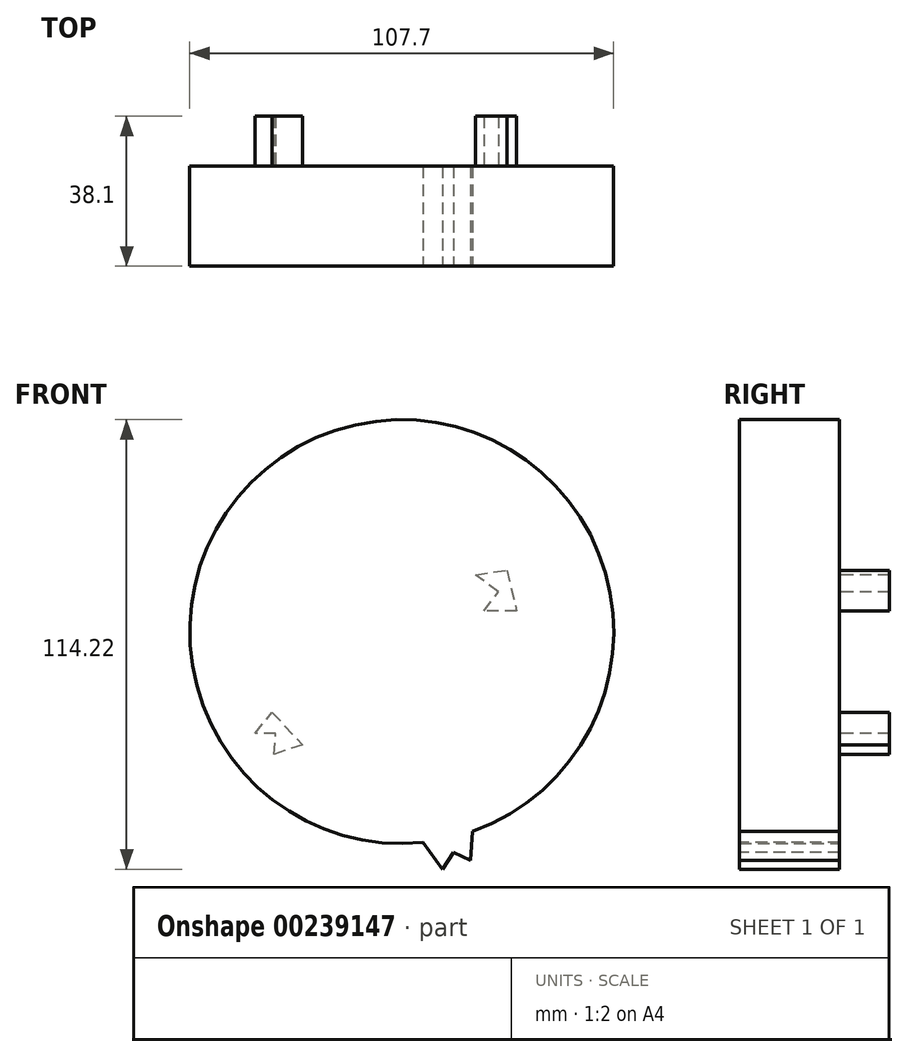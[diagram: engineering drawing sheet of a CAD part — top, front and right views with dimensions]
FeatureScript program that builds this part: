
annotation { "Feature Type Name" : "Feature", "Feature Type Description" : "" }
export const myFeature = defineFeature(function(context is Context, id is Id, definition is map)
    precondition{}
    {
        {
            var Q0;
            Q0=qCreatedBy(makeId("Front.planeOp"),FACE);
            var sketch = newSketch(context, id + "F0", { "sketchPlane" : qUnion([Q0])});
            skCircle(sketch, "E0", {"center": v(0, 0) * mm, "radius": 53.85 * mm});
            skSolve(sketch);
        }
        {
            var Q0;
            Q0 = qSketchRegion(id + "F0", true);
            extrude(context, id + "F1", {"entities" : qUnion([Q0]), "endBound" : BoundingType.SYMMETRIC, "depth" : 25.4 * mm});
        }
        {
            var Q0;
            Q0=makeQuery(id+"F1.opExtrude","CAP_FACE",FACE,{"disambiguationData":[OSD([sQuery(id+"F0.wireOp",EDGE,"E0")])],"isStart":false});
            var sketch = newSketch(context, id + "F2", { "sketchPlane" : qUnion([Q0])});
            skLineSegment(sketch, "E1", {"start": v(17.98, -50.76) * mm, "end": v(5.43, -53.58) * mm});
            skLineSegment(sketch, "E2", {"start": v(5.43, -53.58) * mm, "end": v(10.38, -60.37) * mm});
            skLineSegment(sketch, "E3", {"start": v(10.38, -60.37) * mm, "end": v(13.2, -56.1) * mm});
            skLineSegment(sketch, "E4", {"start": v(13.2, -56.1) * mm, "end": v(17.47, -58.15) * mm});
            skLineSegment(sketch, "E5", {"start": v(17.47, -58.15) * mm, "end": v(17.98, -50.76) * mm});
            skSolve(sketch);
        }
        {
            var Q0;
            Q0 = qSketchRegion(id + "F2", true);
            var Q1;
            Q1=makeQuery(id+"F1.opExtrude","CAP_FACE",FACE,{"disambiguationData":[OSD([sQuery(id+"F0.wireOp",EDGE,"E0")])],"isStart":true});
            extrude(context, id + "F3", {"entities" : qUnion([Q0]), "operationType" : NewBodyOperationType.ADD, "endBound" : BoundingType.UP_TO_SURFACE, "oppositeDirection" : true, "endBoundEntityFace" : qUnion([Q1]), "depth" : 25.4 * mm});
        }
        {
            var Q0;
            {var subQ0=sQuery(id+"F0.wireOp",EDGE,"E0");Q0=makeQuery(id+"FucFUCRXuMYFfXz_1.19.F3.boolean.opBoolean","MERGE",FACE,{"derivedFrom":[makeQuery(id+"FucFUCRXuMYFfXz_1.18.F3.boolean.opBoolean","MERGE",FACE,{"derivedFrom":[makeQuery(id+"FucFUCRXuMYFfXz_1.17.F3.boolean.opBoolean","MERGE",FACE,{"derivedFrom":[makeQuery(id+"FucFUCRXuMYFfXz_1.16.F3.boolean.opBoolean","MERGE",FACE,{"derivedFrom":[makeQuery(id+"FucFUCRXuMYFfXz_1.15.F3.boolean.opBoolean","MERGE",FACE,{"derivedFrom":[makeQuery(id+"FucFUCRXuMYFfXz_1.14.F3.boolean.opBoolean","MERGE",FACE,{"derivedFrom":[makeQuery(id+"FucFUCRXuMYFfXz_1.13.F3.boolean.opBoolean","MERGE",FACE,{"derivedFrom":[makeQuery(id+"FucFUCRXuMYFfXz_1.12.F3.boolean.opBoolean","MERGE",FACE,{"derivedFrom":[makeQuery(id+"FucFUCRXuMYFfXz_1.11.F3.boolean.opBoolean","MERGE",FACE,{"derivedFrom":[makeQuery(id+"FucFUCRXuMYFfXz_1.10.F3.boolean.opBoolean","MERGE",FACE,{"derivedFrom":[makeQuery(id+"FucFUCRXuMYFfXz_1.9.F3.boolean.opBoolean","MERGE",FACE,{"derivedFrom":[makeQuery(id+"FucFUCRXuMYFfXz_1.8.F3.boolean.opBoolean","MERGE",FACE,{"derivedFrom":[makeQuery(id+"FucFUCRXuMYFfXz_1.7.F3.boolean.opBoolean","MERGE",FACE,{"derivedFrom":[makeQuery(id+"FucFUCRXuMYFfXz_1.6.F3.boolean.opBoolean","MERGE",FACE,{"derivedFrom":[makeQuery(id+"FucFUCRXuMYFfXz_1.5.F3.boolean.opBoolean","MERGE",FACE,{"derivedFrom":[makeQuery(id+"FucFUCRXuMYFfXz_1.4.F3.boolean.opBoolean","MERGE",FACE,{"derivedFrom":[makeQuery(id+"FucFUCRXuMYFfXz_1.3.F3.boolean.opBoolean","MERGE",FACE,{"derivedFrom":[makeQuery(id+"FucFUCRXuMYFfXz_1.2.F3.boolean.opBoolean","MERGE",FACE,{"derivedFrom":[makeQuery(id+"FucFUCRXuMYFfXz_1.1.F3.boolean.opBoolean","MERGE",FACE,{"derivedFrom":[makeQuery(id+"F3.boolean.opBoolean","MERGE",FACE,{"derivedFrom":[makeQuery(id+"F1.opExtrude","CAP_FACE",FACE,{"disambiguationData":[OSD([subQ0])],"isStart":true}),makeQuery(id+"F3.opExtrude","CAP_FACE",FACE,{"disambiguationData":[OSD([subQ0])],"isStart":false})]}),makeQuery(id+"FucFUCRXuMYFfXz_1.1.F3.opExtrude","CAP_FACE",FACE,{"disambiguationData":[OSD([subQ0])],"isStart":false})]}),makeQuery(id+"FucFUCRXuMYFfXz_1.2.F3.opExtrude","CAP_FACE",FACE,{"disambiguationData":[OSD([subQ0])],"isStart":false})]}),makeQuery(id+"FucFUCRXuMYFfXz_1.3.F3.opExtrude","CAP_FACE",FACE,{"disambiguationData":[OSD([subQ0])],"isStart":false})]}),makeQuery(id+"FucFUCRXuMYFfXz_1.4.F3.opExtrude","CAP_FACE",FACE,{"disambiguationData":[OSD([subQ0])],"isStart":false})]}),makeQuery(id+"FucFUCRXuMYFfXz_1.5.F3.opExtrude","CAP_FACE",FACE,{"disambiguationData":[OSD([subQ0])],"isStart":false})]}),makeQuery(id+"FucFUCRXuMYFfXz_1.6.F3.opExtrude","CAP_FACE",FACE,{"disambiguationData":[OSD([subQ0])],"isStart":false})]}),makeQuery(id+"FucFUCRXuMYFfXz_1.7.F3.opExtrude","CAP_FACE",FACE,{"disambiguationData":[OSD([subQ0])],"isStart":false})]}),makeQuery(id+"FucFUCRXuMYFfXz_1.8.F3.opExtrude","CAP_FACE",FACE,{"disambiguationData":[OSD([subQ0])],"isStart":false})]}),makeQuery(id+"FucFUCRXuMYFfXz_1.9.F3.opExtrude","CAP_FACE",FACE,{"disambiguationData":[OSD([subQ0])],"isStart":false})]}),makeQuery(id+"FucFUCRXuMYFfXz_1.10.F3.opExtrude","CAP_FACE",FACE,{"disambiguationData":[OSD([subQ0])],"isStart":false})]}),makeQuery(id+"FucFUCRXuMYFfXz_1.11.F3.opExtrude","CAP_FACE",FACE,{"disambiguationData":[OSD([subQ0])],"isStart":false})]}),makeQuery(id+"FucFUCRXuMYFfXz_1.12.F3.opExtrude","CAP_FACE",FACE,{"disambiguationData":[OSD([subQ0])],"isStart":false})]}),makeQuery(id+"FucFUCRXuMYFfXz_1.13.F3.opExtrude","CAP_FACE",FACE,{"disambiguationData":[OSD([subQ0])],"isStart":false})]}),makeQuery(id+"FucFUCRXuMYFfXz_1.14.F3.opExtrude","CAP_FACE",FACE,{"disambiguationData":[OSD([subQ0])],"isStart":false})]}),makeQuery(id+"FucFUCRXuMYFfXz_1.15.F3.opExtrude","CAP_FACE",FACE,{"disambiguationData":[OSD([subQ0])],"isStart":false})]}),makeQuery(id+"FucFUCRXuMYFfXz_1.16.F3.opExtrude","CAP_FACE",FACE,{"disambiguationData":[OSD([subQ0])],"isStart":false})]}),makeQuery(id+"FucFUCRXuMYFfXz_1.17.F3.opExtrude","CAP_FACE",FACE,{"disambiguationData":[OSD([subQ0])],"isStart":false})]}),makeQuery(id+"FucFUCRXuMYFfXz_1.18.F3.opExtrude","CAP_FACE",FACE,{"disambiguationData":[OSD([subQ0])],"isStart":false})]}),makeQuery(id+"FucFUCRXuMYFfXz_1.19.F3.opExtrude","CAP_FACE",FACE,{"disambiguationData":[OSD([subQ0])],"isStart":false})]});}
            var sketch = newSketch(context, id + "F4", { "sketchPlane" : qUnion([Q0])});
            skLineSegment(sketch, "E6", {"start": v(32.04, -25.82) * mm, "end": v(37.22, -25.82) * mm});
            skLineSegment(sketch, "E7", {"start": v(37.22, -25.82) * mm, "end": v(32.9, -20.53) * mm});
            skLineSegment(sketch, "E8", {"start": v(32.9, -20.53) * mm, "end": v(25.24, -28.74) * mm});
            skLineSegment(sketch, "E9", {"start": v(25.24, -28.74) * mm, "end": v(32.47, -31.22) * mm});
            skLineSegment(sketch, "E10", {"start": v(32.47, -31.22) * mm, "end": v(32.04, -25.82) * mm});
            skSolve(sketch);
        }
        {
            var Q0;
            Q0 = qSketchRegion(id + "F4", true);
            extrude(context, id + "F5", {"entities" : qUnion([Q0]), "operationType" : NewBodyOperationType.ADD, "depth" : 12.7 * mm});
        }
        {
            var Q0;
            {var subQ0=sQuery(id+"F0.wireOp",EDGE,"E0");Q0=makeQuery(id+"FucFUCRXuMYFfXz_1.19.F3.boolean.opBoolean","MERGE",FACE,{"derivedFrom":[makeQuery(id+"FucFUCRXuMYFfXz_1.18.F3.boolean.opBoolean","MERGE",FACE,{"derivedFrom":[makeQuery(id+"FucFUCRXuMYFfXz_1.17.F3.boolean.opBoolean","MERGE",FACE,{"derivedFrom":[makeQuery(id+"FucFUCRXuMYFfXz_1.16.F3.boolean.opBoolean","MERGE",FACE,{"derivedFrom":[makeQuery(id+"FucFUCRXuMYFfXz_1.15.F3.boolean.opBoolean","MERGE",FACE,{"derivedFrom":[makeQuery(id+"FucFUCRXuMYFfXz_1.14.F3.boolean.opBoolean","MERGE",FACE,{"derivedFrom":[makeQuery(id+"FucFUCRXuMYFfXz_1.13.F3.boolean.opBoolean","MERGE",FACE,{"derivedFrom":[makeQuery(id+"FucFUCRXuMYFfXz_1.12.F3.boolean.opBoolean","MERGE",FACE,{"derivedFrom":[makeQuery(id+"FucFUCRXuMYFfXz_1.11.F3.boolean.opBoolean","MERGE",FACE,{"derivedFrom":[makeQuery(id+"FucFUCRXuMYFfXz_1.10.F3.boolean.opBoolean","MERGE",FACE,{"derivedFrom":[makeQuery(id+"FucFUCRXuMYFfXz_1.9.F3.boolean.opBoolean","MERGE",FACE,{"derivedFrom":[makeQuery(id+"FucFUCRXuMYFfXz_1.8.F3.boolean.opBoolean","MERGE",FACE,{"derivedFrom":[makeQuery(id+"FucFUCRXuMYFfXz_1.7.F3.boolean.opBoolean","MERGE",FACE,{"derivedFrom":[makeQuery(id+"FucFUCRXuMYFfXz_1.6.F3.boolean.opBoolean","MERGE",FACE,{"derivedFrom":[makeQuery(id+"FucFUCRXuMYFfXz_1.5.F3.boolean.opBoolean","MERGE",FACE,{"derivedFrom":[makeQuery(id+"FucFUCRXuMYFfXz_1.4.F3.boolean.opBoolean","MERGE",FACE,{"derivedFrom":[makeQuery(id+"FucFUCRXuMYFfXz_1.3.F3.boolean.opBoolean","MERGE",FACE,{"derivedFrom":[makeQuery(id+"FucFUCRXuMYFfXz_1.2.F3.boolean.opBoolean","MERGE",FACE,{"derivedFrom":[makeQuery(id+"FucFUCRXuMYFfXz_1.1.F3.boolean.opBoolean","MERGE",FACE,{"derivedFrom":[makeQuery(id+"F3.boolean.opBoolean","MERGE",FACE,{"derivedFrom":[makeQuery(id+"F1.opExtrude","CAP_FACE",FACE,{"disambiguationData":[OSD([subQ0])],"isStart":true}),makeQuery(id+"F3.opExtrude","CAP_FACE",FACE,{"disambiguationData":[OSD([subQ0])],"isStart":false})]}),makeQuery(id+"FucFUCRXuMYFfXz_1.1.F3.opExtrude","CAP_FACE",FACE,{"disambiguationData":[OSD([subQ0])],"isStart":false})]}),makeQuery(id+"FucFUCRXuMYFfXz_1.2.F3.opExtrude","CAP_FACE",FACE,{"disambiguationData":[OSD([subQ0])],"isStart":false})]}),makeQuery(id+"FucFUCRXuMYFfXz_1.3.F3.opExtrude","CAP_FACE",FACE,{"disambiguationData":[OSD([subQ0])],"isStart":false})]}),makeQuery(id+"FucFUCRXuMYFfXz_1.4.F3.opExtrude","CAP_FACE",FACE,{"disambiguationData":[OSD([subQ0])],"isStart":false})]}),makeQuery(id+"FucFUCRXuMYFfXz_1.5.F3.opExtrude","CAP_FACE",FACE,{"disambiguationData":[OSD([subQ0])],"isStart":false})]}),makeQuery(id+"FucFUCRXuMYFfXz_1.6.F3.opExtrude","CAP_FACE",FACE,{"disambiguationData":[OSD([subQ0])],"isStart":false})]}),makeQuery(id+"FucFUCRXuMYFfXz_1.7.F3.opExtrude","CAP_FACE",FACE,{"disambiguationData":[OSD([subQ0])],"isStart":false})]}),makeQuery(id+"FucFUCRXuMYFfXz_1.8.F3.opExtrude","CAP_FACE",FACE,{"disambiguationData":[OSD([subQ0])],"isStart":false})]}),makeQuery(id+"FucFUCRXuMYFfXz_1.9.F3.opExtrude","CAP_FACE",FACE,{"disambiguationData":[OSD([subQ0])],"isStart":false})]}),makeQuery(id+"FucFUCRXuMYFfXz_1.10.F3.opExtrude","CAP_FACE",FACE,{"disambiguationData":[OSD([subQ0])],"isStart":false})]}),makeQuery(id+"FucFUCRXuMYFfXz_1.11.F3.opExtrude","CAP_FACE",FACE,{"disambiguationData":[OSD([subQ0])],"isStart":false})]}),makeQuery(id+"FucFUCRXuMYFfXz_1.12.F3.opExtrude","CAP_FACE",FACE,{"disambiguationData":[OSD([subQ0])],"isStart":false})]}),makeQuery(id+"FucFUCRXuMYFfXz_1.13.F3.opExtrude","CAP_FACE",FACE,{"disambiguationData":[OSD([subQ0])],"isStart":false})]}),makeQuery(id+"FucFUCRXuMYFfXz_1.14.F3.opExtrude","CAP_FACE",FACE,{"disambiguationData":[OSD([subQ0])],"isStart":false})]}),makeQuery(id+"FucFUCRXuMYFfXz_1.15.F3.opExtrude","CAP_FACE",FACE,{"disambiguationData":[OSD([subQ0])],"isStart":false})]}),makeQuery(id+"FucFUCRXuMYFfXz_1.16.F3.opExtrude","CAP_FACE",FACE,{"disambiguationData":[OSD([subQ0])],"isStart":false})]}),makeQuery(id+"FucFUCRXuMYFfXz_1.17.F3.opExtrude","CAP_FACE",FACE,{"disambiguationData":[OSD([subQ0])],"isStart":false})]}),makeQuery(id+"FucFUCRXuMYFfXz_1.18.F3.opExtrude","CAP_FACE",FACE,{"disambiguationData":[OSD([subQ0])],"isStart":false})]}),makeQuery(id+"FucFUCRXuMYFfXz_1.19.F3.opExtrude","CAP_FACE",FACE,{"disambiguationData":[OSD([subQ0])],"isStart":false})]});}
            var sketch = newSketch(context, id + "F6", { "sketchPlane" : qUnion([Q0])});
            skLineSegment(sketch, "E11", {"start": v(-26.74, 15.6) * mm, "end": v(-29.2, 5.3) * mm});
            skLineSegment(sketch, "E12", {"start": v(-29.2, 5.3) * mm, "end": v(-20.88, 5.3) * mm});
            skLineSegment(sketch, "E13", {"start": v(-20.88, 5.3) * mm, "end": v(-24.51, 10.1) * mm});
            skLineSegment(sketch, "E14", {"start": v(-24.51, 10.1) * mm, "end": v(-18.8, 14.42) * mm});
            skLineSegment(sketch, "E15", {"start": v(-18.8, 14.42) * mm, "end": v(-26.74, 15.6) * mm});
            skSolve(sketch);
        }
        {
            var Q0;
            Q0 = qSketchRegion(id + "F6", true);
            extrude(context, id + "F7", {"entities" : qUnion([Q0]), "operationType" : NewBodyOperationType.ADD, "depth" : 12.7 * mm});
        }
    });
